# Revit family: M_Valve_Balancing and Control_MEPcontent_Oventrop_Hydromat DFC 10647
name_source: partatom
category: Pipe Accessories
revit_build: Autodesk Revit 2015 (Build: 20140223_1515(x64)
units: mm (PartAtom-declared; Revit-internal decimal feet)

## types (5) — shared parameters
Angle = 60.00°
Angle 2 = 30.00°
Angle 3 = -60.00°
Article Description = Differential pressure regulator, flanged
Article Type = Hydromat DFC 10647
Bonnet = Color RGB 35-35-35
Bottom_Flange_Radius = 60.023 mm
Bronze = Color RGB 156-122-90
Cast Iron = Color RGB 140-140-140
Content Supplier URL = www.mepcontent.eu
Crank Radius = 80 mm
Custom = No
Description = Differential pressure regulator, flanged
EMCS Version = 2.0
ETIM Article Class = EC011463
Family Version = 10.14
Hb4 = 18 mm  [stored 0.0590551 ft]
Hb5 = 3 mm  [stored 0.00984252 ft]
Hlp1 = 22 mm  [stored 0.0721785 ft]
IFCExportAs = IfcValveType
IFCExportType = PRESSUREREDUCING
Lgt1 = 2 mm  [stored 0.00656168 ft]
MEPcontent Class = VALVE_BALANCING
Manufacturer = Oventrop
Manufacturer URL = http://www.oventrop.de
Model = Hydromat DFC 10647
Pressure Drop = 0.0 Pa
Product Line = Oventrop
R1 = 9 mm  [stored 0.0295276 ft]
R2 = 10.392 mm
Revit Version = 2015
URL = www.stabiplan.com
Up_Flange_Radius = 103 mm
r1 = 2 mm  [stored 0.00656168 ft]
r2 = 3 mm  [stored 0.00984252 ft]

## per-type parameters (varying)
- DN 65: Body_Height=154 mm; CurDst=23.325 mm; Dst1=28 mm  [stored 0.0918635 ft]; DstChk=28 mm  [stored 0.0918635 ft]; FlangeDiameter=185 mm; GTIN=4026755246018; H=191 mm; Hb1=174.36 mm; Hb2=61.035 mm; Hb3=15.259 mm; Hb6=60.308 mm; Height=375 mm; Hlp2=7.775 mm; L2=23.325 mm; Length=290 mm; Lgt2=15.584 mm; Lgt3=34.4 mm; Lgt4=110 mm; Manufacturer Art. No.=1064751; NominalDiameter=65.000 mm; OuterDiameter=76.100 mm; Rad1=69.375 mm; Rad2=92.5 mm; Rad3=43.4 mm; Rad4=40.4 mm  [stored 0.132546 ft]; Rad5=42.9 mm  [stored 0.140748 ft]; Rad6=32.9 mm  [stored 0.10794 ft]; Rad7=44.9 mm; Radius1=32.500 mm; VDst=29.4 mm  [stored 0.0964567 ft]; VHth=50.4 mm
- DN 80: Body_Height=160 mm; CurDst=28.001 mm; Dst1=32 mm  [stored 0.104987 ft]; DstChk=32 mm  [stored 0.104987 ft]; FlangeDiameter=200 mm; GTIN=4026755246025; H=206 mm; Hb1=191.68 mm; Hb2=73.679 mm; Hb3=18.42 mm; Hb6=73.308 mm; Height=395 mm; Hlp2=9.334 mm; L2=28.001 mm; Length=310 mm; Lgt2=16.088 mm  [stored 0.0527822 ft]; Lgt3=37.1 mm  [stored 0.121719 ft]; Lgt4=110 mm; Manufacturer Art. No.=1064752; NominalDiameter=80.000 mm; OuterDiameter=88.900 mm; Rad1=75 mm; Rad2=100 mm; Rad3=51.5 mm; Rad4=48.5 mm; Rad5=51 mm; Rad6=41 mm; Rad7=53 mm; Radius1=40.000 mm; VDst=32.1 mm; VHth=58.5 mm
- DN 100: Body_Height=134 mm; CurDst=34.237 mm; Dst1=28 mm  [stored 0.0918635 ft]; DstChk=28 mm  [stored 0.0918635 ft]; FlangeDiameter=220 mm; GTIN=4026755301076; H=243 mm; Hb1=234.404 mm; Hb2=110.167 mm; Hb3=27.542 mm; Hb6=112.308 mm; Height=410 mm; Hlp2=11.412 mm; L2=34.237 mm; Length=350 mm; Lgt2=16.76 mm  [stored 0.0549869 ft]; Lgt3=40.7 mm  [stored 0.13353 ft]; Lgt4=110 mm; Manufacturer Art. No.=1064753; NominalDiameter=100.000 mm; OuterDiameter=114.300 mm; Rad1=82.5 mm; Rad2=110 mm; Rad3=62.3 mm; Rad4=59.3 mm; Rad5=61.8 mm; Rad6=51.8 mm; Rad7=63.8 mm; Radius1=50.000 mm; VDst=35.7 mm  [stored 0.117126 ft]; VHth=69.3 mm
- DN 125: Body_Height=131 mm; CurDst=42.031 mm; Dst1=25 mm  [stored 0.082021 ft]; DstChk=25 mm  [stored 0.082021 ft]; FlangeDiameter=250 mm; GTIN=4026755333145; H=286 mm; Hb1=284.056 mm; Hb2=152.025 mm; Hb3=38.006 mm; Hb6=156.808 mm; Height=450 mm; Hlp2=14.01 mm; L2=42.031 mm; Length=400 mm; Lgt2=17.6 mm  [stored 0.0577428 ft]; Lgt3=45.2 mm; Lgt4=157.5 mm; Manufacturer Art. No.=1064754; NominalDiameter=125.000 mm; OuterDiameter=139.700 mm; Rad1=93.75 mm; Rad2=125 mm; Rad3=75.8 mm; Rad4=72.8 mm; Rad5=75.3 mm; Rad6=65.3 mm; Rad7=77.3 mm; Radius1=62.500 mm; VDst=40.2 mm; VHth=82.8 mm
- DN 150: Body_Height=128 mm; CurDst=49.825 mm; Dst1=40 mm  [stored 0.131234 ft]; DstChk=40 mm  [stored 0.131234 ft]; FlangeDiameter=285 mm; GTIN=4026755333152; H=288 mm; Hb1=286.366 mm; Hb2=146.54 mm; Hb3=36.635 mm; Hb6=151.308 mm; Height=450 mm; Hlp2=16.608 mm; L2=49.825 mm; Length=480 mm; Lgt2=18.44 mm  [stored 0.0604987 ft]; Lgt3=49.7 mm; Lgt4=205 mm; Manufacturer Art. No.=1064755; NominalDiameter=150.000 mm; OuterDiameter=168.300 mm; Rad1=106.875 mm; Rad2=142.5 mm; Rad3=89.3 mm; Rad4=86.3 mm; Rad5=88.8 mm; Rad6=78.8 mm; Rad7=90.8 mm; Radius1=75.000 mm; VDst=44.7 mm; VHth=96.3 mm

note: [stored X ft] marks values corroborated as IEEE doubles in the binary element streams (Revit-internal decimal feet)

## geometry (parser evidence)
native form markers: Blend x4, Sweep x4
no freeform markers — native parametric forms only
